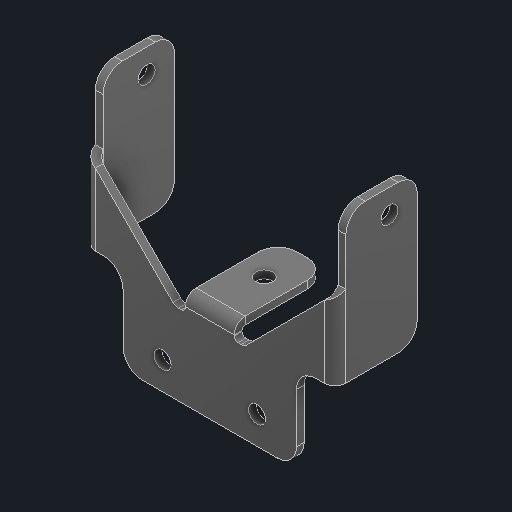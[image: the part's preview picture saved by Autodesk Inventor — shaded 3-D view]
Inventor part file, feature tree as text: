
AUTODESK INVENTOR PART (.ipt)
format: ipt  version: 2024 (Build 280153000, 153)  size: 156,160 bytes
history: native  units: in
note: dims shown in document units (in); Inventor stores cm internally (conversion verified against a paired STEP export)
features: fillet x1
ambient origin geometry x8: Origin, YZ Plane, XZ Plane, XY Plane, X Axis, Y Axis, Z Axis, Center Point
bodies: Solid1 (feature_tree)
feature tree (1):
  fillet  "Fillet5"  [1 undecoded]
note: 1 required parameter value undecoded (feature->parameter linkage not recoverable at this tier; creation-order binding heuristic only, values carry confidence <= 0.55)
